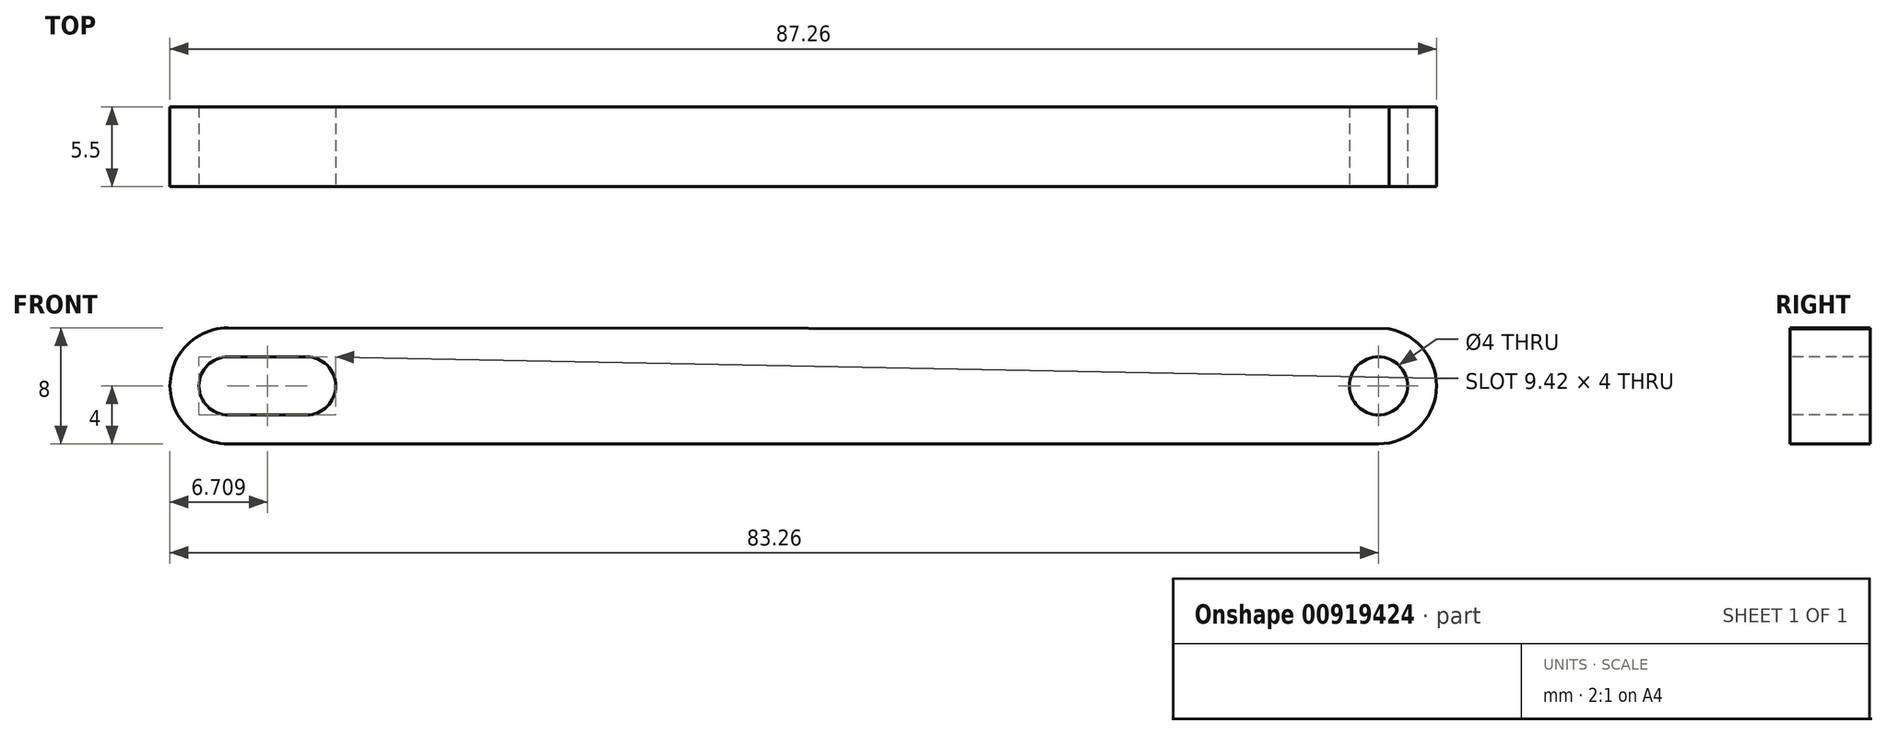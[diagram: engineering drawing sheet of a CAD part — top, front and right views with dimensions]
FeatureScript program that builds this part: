
annotation { "Feature Type Name" : "Feature", "Feature Type Description" : "" }
export const myFeature = defineFeature(function(context is Context, id is Id, definition is map)
    precondition{}
    {
        {
            var Q0;
            Q0=qCreatedBy(makeId("Front.planeOp"),FACE);
            var sketch = newSketch(context, id + "F0", { "sketchPlane" : qUnion([Q0])});
            skCircle(sketch, "E0", {"center": v(0, 0) * mm, "radius": 4 * mm});
            skCircle(sketch, "E1", {"center": v(-79.26, 0) * mm, "radius": 4 * mm});
            skLineSegment(sketch, "E2", {"start": v(-79.26, 4) * mm, "end": v(0.74, 3.93) * mm});
            skLineSegment(sketch, "E3", {"start": v(-79.26, -4) * mm, "end": v(0, -4) * mm});
            skSolve(sketch);
        }
        {
            var Q0;
            {var subQ0=sQuery(id+"F0.wireOp",EDGE,"E3");Q0=makeQuery(id+"F0.imprint","IMPRINT",FACE,{"disambiguationData":[TD([[makeQuery(id+"F0.imprint","IMPRINT",EDGE,{"derivedFrom":subQ0}),1.0]])]});}
            var Q1;
            {var subQ0=sQuery(id+"F0.wireOp",EDGE,"E1");var subQ1=makeQuery(id+"F0.imprint","INTERSECT",VERTEX,{"derivedFrom":[subQ0,sQuery(id+"F0.wireOp",EDGE,"E2")]});Q1=makeQuery(id+"F0.imprint","IMPRINT",FACE,{"disambiguationData":[TD([[makeQuery(id+"F0.imprint","IMPRINT",EDGE,{"disambiguationData":[TD([[subQ1,-1.0]])],"derivedFrom":subQ0}),1.0]])]});}
            var Q2;
            {var subQ0=sQuery(id+"F0.wireOp",EDGE,"E0");var subQ1=makeQuery(id+"F0.imprint","INTERSECT",VERTEX,{"derivedFrom":[subQ0,sQuery(id+"F0.wireOp",EDGE,"E3")]});Q2=makeQuery(id+"F0.imprint","IMPRINT",FACE,{"disambiguationData":[TD([[makeQuery(id+"F0.imprint","IMPRINT",EDGE,{"disambiguationData":[TD([[subQ1,1.0]])],"derivedFrom":subQ0}),1.0]])]});}
            extrude(context, id + "F1", {"entities" : qUnion([Q0, Q1, Q2]), "depth" : 5.5 * mm, "offsetDistance" : 25 * mm});
        }
        {
            var Q0;
            Q0=makeQuery(id+"F1.opExtrude","CAP_FACE",FACE,{"disambiguationData":[OSD([sQuery(id+"F0.wireOp",EDGE,"E0"),sQuery(id+"F0.wireOp",EDGE,"E1"),sQuery(id+"F0.wireOp",EDGE,"E2"),sQuery(id+"F0.wireOp",EDGE,"E3")])],"isStart":false});
            var sketch = newSketch(context, id + "F2", { "sketchPlane" : qUnion([Q0])});
            skCircle(sketch, "E4", {"center": v(0, 0) * mm, "radius": 2 * mm});
            skCircle(sketch, "E5", {"center": v(-79.26, 0) * mm, "radius": 2 * mm});
            skCircle(sketch, "E6", {"center": v(-73.84, 0) * mm, "radius": 2 * mm});
            skLineSegment(sketch, "E7", {"start": v(-79.26, 2) * mm, "end": v(-73.84, 2) * mm});
            skLineSegment(sketch, "E8", {"start": v(-79.26, -2) * mm, "end": v(-73.84, -2) * mm});
            skSolve(sketch);
        }
        {
            var Q0;
            {var subQ0=sQuery(id+"F2.wireOp",EDGE,"E5");var subQ1=makeQuery(id+"F2.imprint","INTERSECT",VERTEX,{"derivedFrom":[subQ0,sQuery(id+"F2.wireOp",EDGE,"E7")]});Q0=makeQuery(id+"F2.imprint","IMPRINT",FACE,{"disambiguationData":[TD([[makeQuery(id+"F2.imprint","IMPRINT",EDGE,{"disambiguationData":[TD([[subQ1,-1.0]])],"derivedFrom":subQ0}),1.0]])]});}
            var Q1;
            {var subQ0=sQuery(id+"F2.wireOp",EDGE,"E7");Q1=makeQuery(id+"F2.imprint","IMPRINT",FACE,{"disambiguationData":[TD([[makeQuery(id+"F2.imprint","IMPRINT",EDGE,{"derivedFrom":subQ0}),-1.0]])]});}
            var Q2;
            {var subQ0=sQuery(id+"F2.wireOp",EDGE,"E6");var subQ1=makeQuery(id+"F2.imprint","INTERSECT",VERTEX,{"derivedFrom":[subQ0,sQuery(id+"F2.wireOp",EDGE,"E7")]});Q2=makeQuery(id+"F2.imprint","IMPRINT",FACE,{"disambiguationData":[TD([[makeQuery(id+"F2.imprint","IMPRINT",EDGE,{"disambiguationData":[TD([[subQ1,-1.0]])],"derivedFrom":subQ0}),1.0]])]});}
            var Q3;
            Q3=makeQuery(id+"F2.imprint","IMPRINT",FACE,{"disambiguationData":[TD([[makeQuery(id+"F2.imprint","IMPRINT",EDGE,{"derivedFrom":sQuery(id+"F2.wireOp",EDGE,"E4")}),1.0]])]});
            extrude(context, id + "F3", {"entities" : qUnion([Q0, Q1, Q2, Q3]), "operationType" : NewBodyOperationType.REMOVE, "oppositeDirection" : true, "depth" : 25 * mm, "offsetDistance" : 25 * mm});
        }
    });
